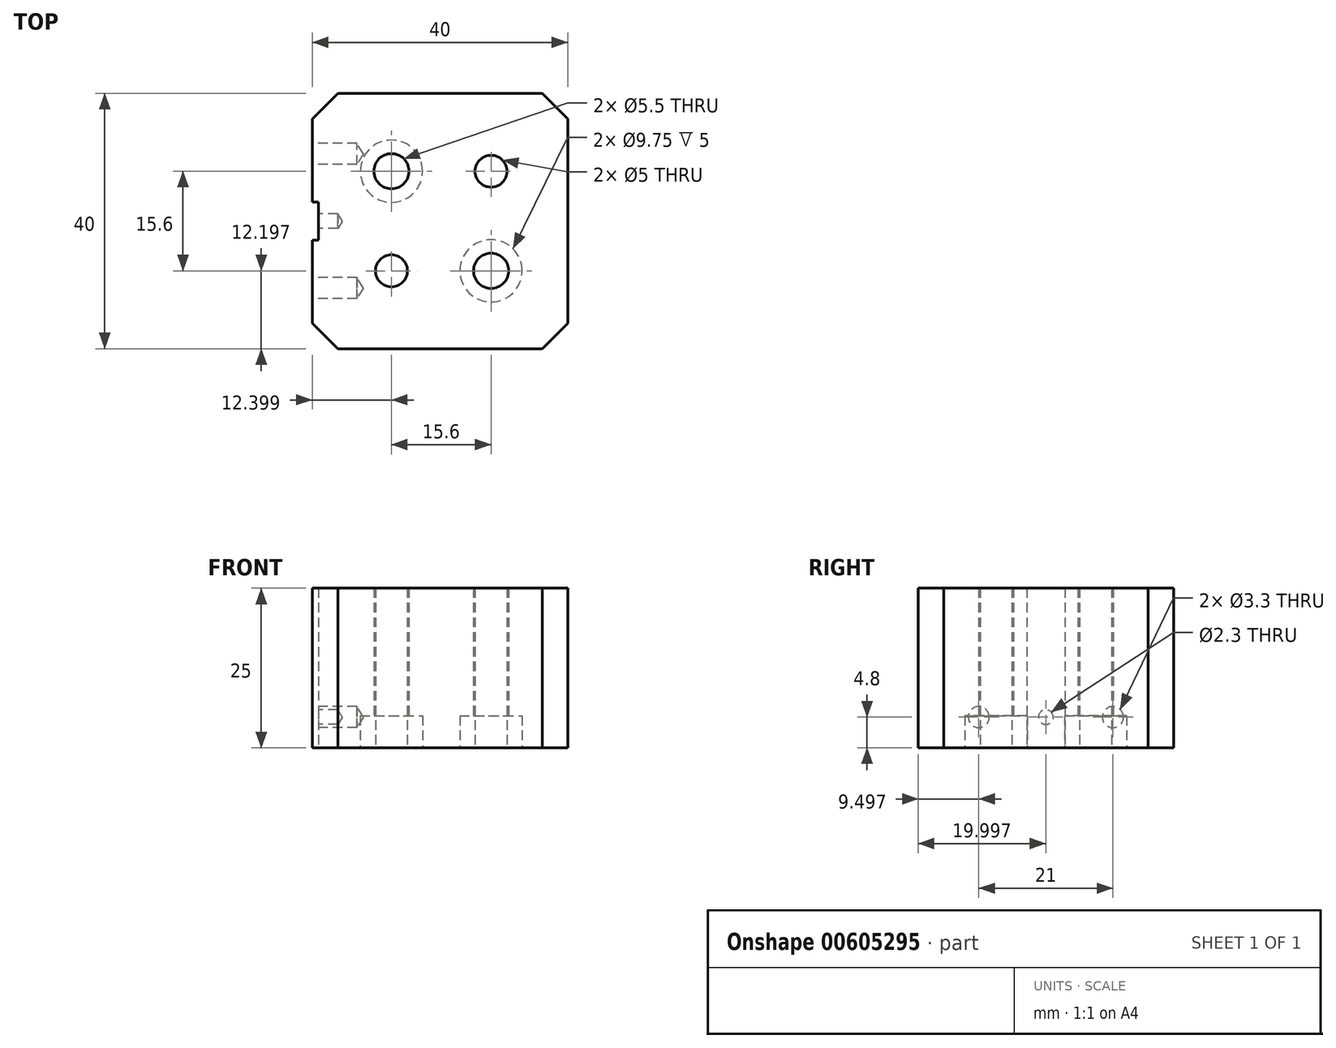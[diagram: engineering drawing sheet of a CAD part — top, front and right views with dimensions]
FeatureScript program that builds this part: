
annotation { "Feature Type Name" : "Feature", "Feature Type Description" : "" }
export const myFeature = defineFeature(function(context is Context, id is Id, definition is map)
    precondition{}
    {
        {
            var Q0;
            Q0=qCreatedBy(makeId("Top.planeOp"),FACE);
            var sketch = newSketch(context, id + "F0", { "sketchPlane" : qUnion([Q0])});
            skLineSegment(sketch, "E0.bottom", {"start": v(-5.4, 12.05) * mm, "end": v(34.6, 12.05) * mm});
            skLineSegment(sketch, "E0.top", {"start": v(-5.4, -27.95) * mm, "end": v(34.6, -27.95) * mm});
            skLineSegment(sketch, "E0.left", {"start": v(-5.4, 12.05) * mm, "end": v(-5.4, -27.95) * mm});
            skLineSegment(sketch, "E0.right", {"start": v(34.6, 12.05) * mm, "end": v(34.6, -27.95) * mm});
            skPoint(sketch, "E1", {"position": v(22.6, -0.15) * mm});
            skPoint(sketch, "E2", {"position": v(7, -0.15) * mm});
            skPoint(sketch, "E3", {"position": v(22.6, -15.75) * mm});
            skPoint(sketch, "E4", {"position": v(7, -15.75) * mm});
            skLineSegment(sketch, "E5.bottom", {"start": v(-4.4, -10.95) * mm, "end": v(-6.4, -10.95) * mm});
            skLineSegment(sketch, "E5.top", {"start": v(-4.4, -4.95) * mm, "end": v(-6.4, -4.95) * mm});
            skLineSegment(sketch, "E5.left", {"start": v(-4.4, -10.95) * mm, "end": v(-4.4, -4.95) * mm});
            skLineSegment(sketch, "E5.right", {"start": v(-6.4, -10.95) * mm, "end": v(-6.4, -4.95) * mm});
            skPoint(sketch, "E5.middle", {"position": v(-5.4, -7.95) * mm});
            skSolve(sketch);
        }
        {
            var Q0;
            Q0=makeQuery(id+"F0.imprint","IMPRINT",FACE,{"disambiguationData":[TD([[makeQuery(id+"F0.imprint","IMPRINT",EDGE,{"derivedFrom":sQuery(id+"F0.wireOp",EDGE,"E0.bottom")}),-1.0]])]});
            extrude(context, id + "F1", {"entities" : qUnion([Q0]), "depth" : 25 * mm, "offsetDistance" : 25 * mm});
        }
        {
            var Q0;
            Q0=makeQuery(id+"F1.opExtrude","SWEPT_EDGE",EDGE,{"disambiguationData":[OSD([sQuery(id+"F0.wireOp",EDGE,"E0.bottom"),sQuery(id+"F0.wireOp",EDGE,"E0.left")])]});
            var Q1;
            Q1=makeQuery(id+"F1.opExtrude","SWEPT_EDGE",EDGE,{"disambiguationData":[OSD([sQuery(id+"F0.wireOp",EDGE,"E0.top"),sQuery(id+"F0.wireOp",EDGE,"E0.left")])]});
            var Q2;
            Q2=makeQuery(id+"F1.opExtrude","SWEPT_EDGE",EDGE,{"disambiguationData":[OSD([sQuery(id+"F0.wireOp",EDGE,"E0.top"),sQuery(id+"F0.wireOp",EDGE,"E0.right")])]});
            var Q3;
            Q3=makeQuery(id+"F1.opExtrude","SWEPT_EDGE",EDGE,{"disambiguationData":[OSD([sQuery(id+"F0.wireOp",EDGE,"E0.bottom"),sQuery(id+"F0.wireOp",EDGE,"E0.right")])]});
            chamfer(context, id + "F2", {"entities" : qUnion([Q0, Q1, Q2, Q3]), "chamferType" : ChamferType.OFFSET_ANGLE, "width" : 4 * mm, "oppositeDirection" : false, "angle" : 45 * degree, "tangentPropagation" : true});
        }
        {
            var Q0;
            Q0=sQuery(id+"F0.wireOp",VERTEX,"E2");
            var Q1;
            Q1=makeQuery(id+"F1.opExtrude","SWEPT_BODY",BODY,{"disambiguationData":[OSD([sQuery(id+"F0.wireOp",EDGE,"E0.bottom"),sQuery(id+"F0.wireOp",EDGE,"E0.top"),sQuery(id+"F0.wireOp",EDGE,"E0.left"),sQuery(id+"F0.wireOp",EDGE,"E0.right")])]});
            hole(context, id + "F3", {"style" : HoleStyle.C_BORE, "endStyle" : HoleEndStyle.THROUGH, "oppositeDirection" : true, "standardTappedOrClearance" : lookupTablePath({ "standard" : "ISO", "fit" : "Normal", "size" : "M5", "type" : "Clearance" }), "standardBlindInLast" : lookupTablePath({ "fit" : "Standard", "standard" : "ISO", "size" : "M5", "type" : "Clearance" }), "holeDiameter" : 5.5 * mm, "cBoreDiameter" : 9.75 * mm, "cBoreDepth" : 5 * mm, "majorDiameter" : 5 * mm, "isTappedThrough" : true, "tappedDepth" : 17.9 * mm, "tapClearance" : 3, "locations" : qUnion([Q0]), "scope" : qUnion([Q1])});
        }
        {
            var Q0;
            Q0=sQuery(id+"F0.wireOp",VERTEX,"E3");
            var Q1;
            Q1=makeQuery(id+"F1.opExtrude","SWEPT_BODY",BODY,{"disambiguationData":[OSD([sQuery(id+"F0.wireOp",EDGE,"E0.bottom"),sQuery(id+"F0.wireOp",EDGE,"E0.top"),sQuery(id+"F0.wireOp",EDGE,"E0.left"),sQuery(id+"F0.wireOp",EDGE,"E0.right"),sQuery(id+"F0.wireOp",EDGE,"E5.bottom"),sQuery(id+"F0.wireOp",EDGE,"E5.top"),sQuery(id+"F0.wireOp",EDGE,"E5.left")])]});
            hole(context, id + "F4", {"style" : HoleStyle.C_BORE, "endStyle" : HoleEndStyle.THROUGH, "oppositeDirection" : true, "standardTappedOrClearance" : lookupTablePath({ "standard" : "ISO", "fit" : "Normal", "size" : "M5", "type" : "Clearance" }), "standardBlindInLast" : lookupTablePath({ "fit" : "Standard", "standard" : "ISO", "size" : "M5", "type" : "Clearance" }), "holeDiameter" : 5.5 * mm, "cBoreDiameter" : 9.75 * mm, "cBoreDepth" : 5 * mm, "majorDiameter" : 5 * mm, "isTappedThrough" : true, "tappedDepth" : 17.9 * mm, "tapClearance" : 3, "locations" : qUnion([Q0]), "scope" : qUnion([Q1])});
        }
        {
            var Q0;
            Q0=sQuery(id+"F0.wireOp",VERTEX,"E1");
            var Q1;
            Q1=makeQuery(id+"F1.opExtrude","SWEPT_BODY",BODY,{"disambiguationData":[OSD([sQuery(id+"F0.wireOp",EDGE,"E0.bottom"),sQuery(id+"F0.wireOp",EDGE,"E0.top"),sQuery(id+"F0.wireOp",EDGE,"E0.left"),sQuery(id+"F0.wireOp",EDGE,"E0.right"),sQuery(id+"F0.wireOp",EDGE,"E5.bottom"),sQuery(id+"F0.wireOp",EDGE,"E5.top"),sQuery(id+"F0.wireOp",EDGE,"E5.left")])]});
            hole(context, id + "F5", {"style" : HoleStyle.SIMPLE, "endStyle" : HoleEndStyle.THROUGH, "oppositeDirection" : true, "holeDiameter" : 5 * mm, "majorDiameter" : 5 * mm, "isTappedThrough" : true, "tappedDepth" : 17.9 * mm, "tapClearance" : 3, "locations" : qUnion([Q0]), "scope" : qUnion([Q1])});
        }
        {
            var Q0;
            Q0=sQuery(id+"F0.wireOp",VERTEX,"E4");
            var Q1;
            Q1=makeQuery(id+"F1.opExtrude","SWEPT_BODY",BODY,{"disambiguationData":[OSD([sQuery(id+"F0.wireOp",EDGE,"E0.bottom"),sQuery(id+"F0.wireOp",EDGE,"E0.top"),sQuery(id+"F0.wireOp",EDGE,"E0.left"),sQuery(id+"F0.wireOp",EDGE,"E0.right"),sQuery(id+"F0.wireOp",EDGE,"E5.bottom"),sQuery(id+"F0.wireOp",EDGE,"E5.top"),sQuery(id+"F0.wireOp",EDGE,"E5.left")])]});
            hole(context, id + "F6", {"style" : HoleStyle.SIMPLE, "endStyle" : HoleEndStyle.THROUGH, "oppositeDirection" : true, "holeDiameter" : 5 * mm, "majorDiameter" : 5 * mm, "isTappedThrough" : true, "tappedDepth" : 17.9 * mm, "tapClearance" : 3, "locations" : qUnion([Q0]), "scope" : qUnion([Q1])});
        }
        {
            var Q0;
            {var subQ0=sQuery(id+"F0.wireOp",EDGE,"E0.left");Q0=makeQuery(id+"F1.opExtrude","SWEPT_FACE",FACE,{"disambiguationData":[OSD([subQ0]),TDD([makeQuery(id+"F0.imprint","IMPRINT",EDGE,{"disambiguationData":[TD([[makeQuery(id+"F0.imprint","INTERSECT",VERTEX,{"derivedFrom":[sQuery(id+"F0.wireOp",EDGE,"E0.bottom"),subQ0]}),-1.0]])],"derivedFrom":subQ0})])]});}
            var sketch = newSketch(context, id + "F7", { "sketchPlane" : qUnion([Q0])});
            skPoint(sketch, "E6", {"position": v(-2.55, 4.8) * mm});
            skPoint(sketch, "E7", {"position": v(18.45, 4.8) * mm});
            skSolve(sketch);
        }
        {
            var Q0;
            Q0=makeQuery(id+"F1.opExtrude","SWEPT_FACE",FACE,{"disambiguationData":[OSD([sQuery(id+"F0.wireOp",EDGE,"E5.left")])]});
            var sketch = newSketch(context, id + "F8", { "sketchPlane" : qUnion([Q0])});
            skPoint(sketch, "E8", {"position": v(7.95, 4.8) * mm});
            skPoint(sketch, "E8.positionSnap0", {"position": v(7.95, 0) * mm});
            skSolve(sketch);
        }
        {
            var Q0;
            Q0=sQuery(id+"F7.wireOp",VERTEX,"E6");
            var Q1;
            Q1=sQuery(id+"F7.wireOp",VERTEX,"E7");
            var Q2;
            Q2=makeQuery(id+"F1.opExtrude","SWEPT_BODY",BODY,{"disambiguationData":[OSD([sQuery(id+"F0.wireOp",EDGE,"E0.bottom"),sQuery(id+"F0.wireOp",EDGE,"E0.top"),sQuery(id+"F0.wireOp",EDGE,"E0.left"),sQuery(id+"F0.wireOp",EDGE,"E0.right"),sQuery(id+"F0.wireOp",EDGE,"E5.bottom"),sQuery(id+"F0.wireOp",EDGE,"E5.top"),sQuery(id+"F0.wireOp",EDGE,"E5.left")])]});
            hole(context, id + "F9", {"style" : HoleStyle.SIMPLE, "endStyle" : HoleEndStyle.BLIND, "holeDiameter" : 3.3 * mm, "majorDiameter" : 5 * mm, "holeDepth" : 7 * mm, "isTappedThrough" : true, "tappedDepth" : 17.9 * mm, "tapClearance" : 3, "locations" : qUnion([Q0, Q1]), "scope" : qUnion([Q2])});
        }
        {
            var Q0;
            Q0=sQuery(id+"F8.wireOp",VERTEX,"E8");
            var Q1;
            Q1=makeQuery(id+"F1.opExtrude","SWEPT_BODY",BODY,{"disambiguationData":[OSD([sQuery(id+"F0.wireOp",EDGE,"E0.bottom"),sQuery(id+"F0.wireOp",EDGE,"E0.top"),sQuery(id+"F0.wireOp",EDGE,"E0.left"),sQuery(id+"F0.wireOp",EDGE,"E0.right"),sQuery(id+"F0.wireOp",EDGE,"E5.bottom"),sQuery(id+"F0.wireOp",EDGE,"E5.top"),sQuery(id+"F0.wireOp",EDGE,"E5.left")])]});
            hole(context, id + "F10", {"style" : HoleStyle.SIMPLE, "endStyle" : HoleEndStyle.BLIND, "holeDiameter" : 2.3 * mm, "majorDiameter" : 5 * mm, "holeDepth" : 3 * mm, "isTappedThrough" : true, "tappedDepth" : 17.9 * mm, "tapClearance" : 3, "locations" : qUnion([Q0]), "scope" : qUnion([Q1])});
        }
    });
